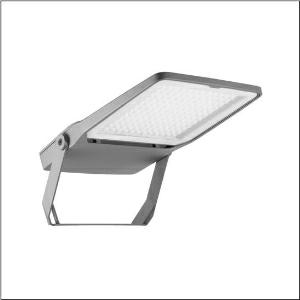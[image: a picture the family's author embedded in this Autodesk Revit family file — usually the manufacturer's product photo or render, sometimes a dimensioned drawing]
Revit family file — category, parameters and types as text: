
# Revit family: floodlight_fl_20_midi___pl43_5xa7681e2a1ac_2bcd
name_source: partatom
category: Lighting Fixtures
units: mm (PartAtom-declared; Revit-internal decimal feet)

## family parameters
Cut with Voids When Loaded = No
Host = Face
Light Source = No
Part Type = Normal
Room Calculation Point = No
Round Connector Dimension = Use Diameter
Shared = No

## types (1)
- Floodlight FL 20 midi  PL43 (1 x LED 4000K / CRI = 70 (unbekannt), 28460 lm, 4000K)
    Apparent Load = 208 VA
    CIE Flux Codes = 32 74 99 100 100
    Color Rendering = 70
    Color Temperature = 4000K
    Default Elevation = 1800 mm
    Description = Floodlight FL 20 midi, floodlight, primary light control with lens, of plastic, primary optical cover: protective disc, of toughened safety glass, transparent, light distribution: PL43, light emission: direct distribution, primary light characteristic: asymmetric, installation type: surface-mounted, LED, High Power LED, rated luminous flux: 28.460lm, luminous efficacy: 137lm/W, light colour: 740, colour temperature: 4000K, control gear: ECG Basic, control: power reduction, overheat protection, electronic power reduction, with terminal, 5-pole, max. 2.5mm², mains connection: 220..240V, AC, 50/60Hz, rated input power: 208W, LED unit, of diecast aluminium, powder-coated, Siteco® metallic grey (DB 702S), corrosivity category C5 mid according to DIN EN ISO 12944, incl. 1x M20 cable gland for cable Ø 6.5..12mm, length: 654mm, width: 450mm, height: 76mm, housing frame, of diecast aluminium, powder-coated, Siteco® metallic grey (DB 702S), mounting bracket, of steel, powder-coated, Siteco® metallic grey (DB 702S), ON/OFF, protection rating (complete): IP66, insulation class (complete): insulation class I (protective earthing), certification: CE, ENEC, VDE, protection symbol: D, permissible operating ambient temperature: -40..+40°C, permissible operating ambient temperature for outdoor applications: -40..+50°C, standard: DIN EN 12944, packaging unit: 1 piece

Light Distribution: PL43
    Height = 76 mm
    Lamp = 1 x LED 4000K / CRI >= 70 (unbekannt)
    Lamp Light Flux = 28460 lm
    Lamp count = 1
    Length = 672 mm
    Luminous efficacy = 137 lm/W
    Manufacturer = Siteco
    ModVariant = No
    Model = 5XA7681E2A1AC
    Mounting Place = Wall
    Mounting Type = Surface mounted
    Number of Poles = 1
    OnlyDefault = Yes
    Power Factor = 1
    Product Name = Floodlight FL 20 midi | PL43
    Product group = floodlight | wall mounted
    ProductGroupID = 2001
    Protection Class = Protection class I
    Protection Degree = IP 66
    RLX_Detail_Level = 1
    RLX_Emergency_Light_Flux = 0 lm
    RLX_Emergency_Type = 0
    RLX_Emergency_Type_DB = No
    RlxData = <blob elided: 94057 chars, md5=a43efdb2>
    Socket = socket
    Standby Power = 0 W
    System Light Flux = 28460 lm
    System Power = 208 W
    Type Comments = Product without accessories
    Type Image = l_1005943.jpg
    URL = http://relux.com
    VarID = ---
    Voltage = 0 V
    Weight = 0.00 kg
    Width = 450 mm

## geometry (parser evidence)
native form markers: Blend x4, Sweep x15
no freeform markers — native parametric forms only
